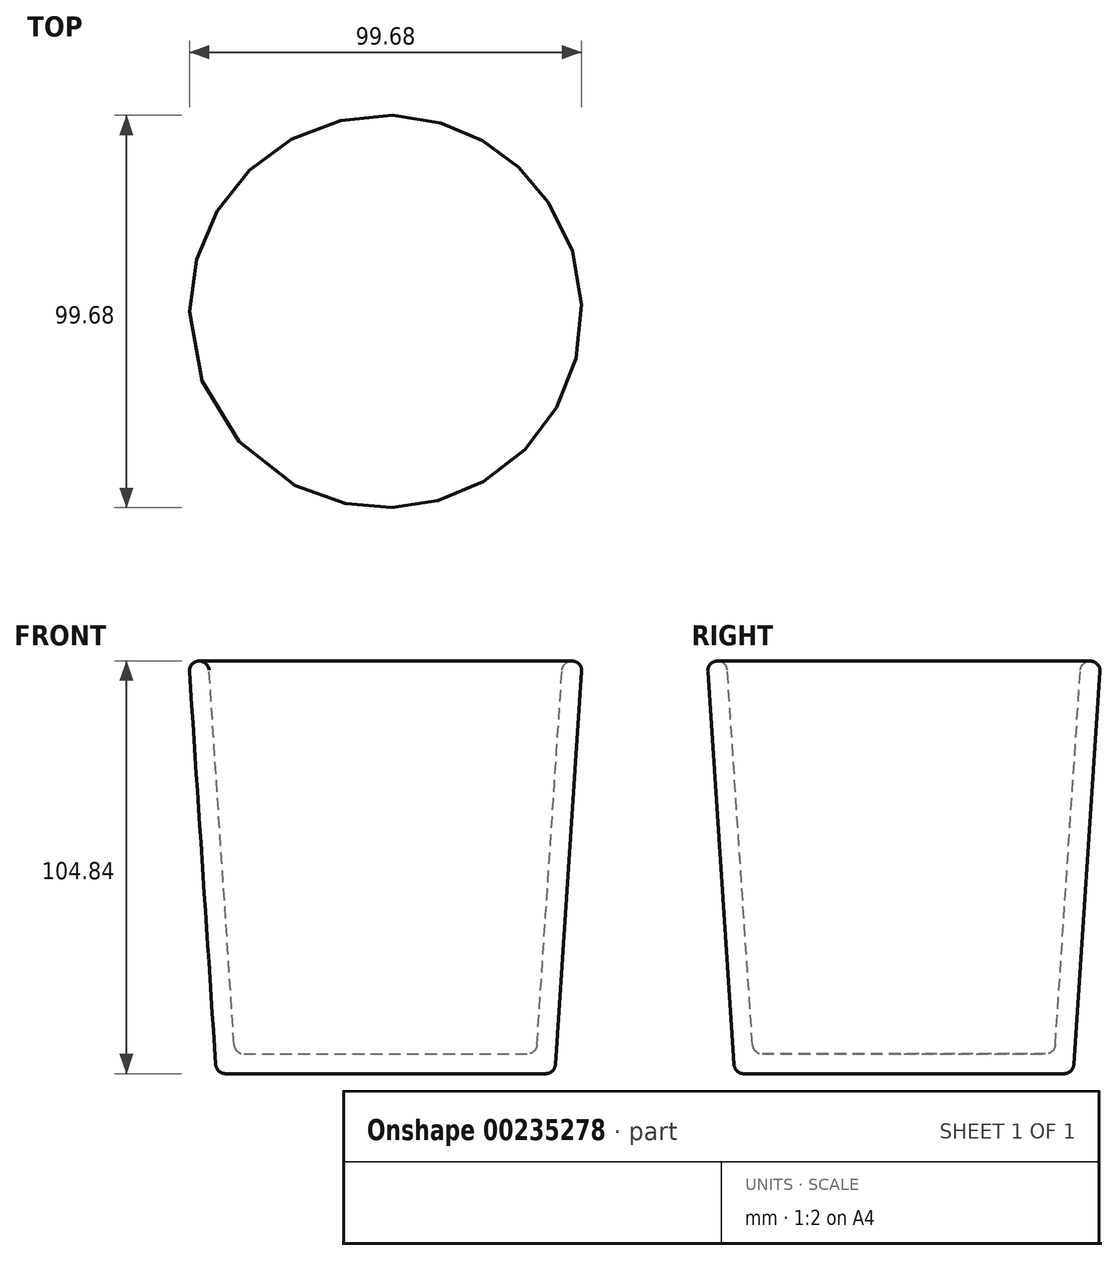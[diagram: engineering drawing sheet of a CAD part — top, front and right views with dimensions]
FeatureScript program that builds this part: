
annotation { "Feature Type Name" : "Feature", "Feature Type Description" : "" }
export const myFeature = defineFeature(function(context is Context, id is Id, definition is map)
    precondition{}
    {
        {
            var Q0;
            Q0=qCreatedBy(makeId("Front.planeOp"),FACE);
            var sketch = newSketch(context, id + "F0", { "sketchPlane" : qUnion([Q0])});
            skLineSegment(sketch, "E0", {"start": v(0, 0) * mm, "end": v(43, 0) * mm});
            skLineSegment(sketch, "E1", {"start": v(43, 0) * mm, "end": v(50, 104.67) * mm});
            skLineSegment(sketch, "E2", {"start": v(50, 104.67) * mm, "end": v(45.01, 105) * mm});
            skLineSegment(sketch, "E3", {"start": v(45.01, 105) * mm, "end": v(38.32, 5) * mm});
            skLineSegment(sketch, "E4", {"start": v(38.32, 5) * mm, "end": v(0, 5) * mm});
            skLineSegment(sketch, "E5", {"start": v(0, 5) * mm, "end": v(0, 0) * mm});
            skSolve(sketch);
        }
        {
            var Q0;
            Q0 = qSketchRegion(id + "F0", true);
            var Q1;
            Q1=sQuery(id+"F0.wireOp",EDGE,"E5");
            revolve(context, id + "F1", {"entities" : qUnion([Q0]), "axis" : qUnion([Q1]), "revolveType" : RevolveType.FULL});
        }
        {
            var Q0;
            Q0=makeQuery(id+"F1.opRevolve","SWEPT_EDGE",EDGE,{"disambiguationData":[OSD([sQuery(id+"F0.wireOp",EDGE,"E1"),sQuery(id+"F0.wireOp",EDGE,"E2")])]});
            var Q1;
            Q1=makeQuery(id+"F1.opRevolve","SWEPT_EDGE",EDGE,{"disambiguationData":[OSD([sQuery(id+"F0.wireOp",EDGE,"E2"),sQuery(id+"F0.wireOp",EDGE,"E3")])]});
            var Q2;
            Q2=makeQuery(id+"F1.opRevolve","SWEPT_EDGE",EDGE,{"disambiguationData":[OSD([sQuery(id+"F0.wireOp",EDGE,"E0"),sQuery(id+"F0.wireOp",EDGE,"E1")])]});
            var Q3;
            Q3=makeQuery(id+"F1.opRevolve","SWEPT_EDGE",EDGE,{"disambiguationData":[OSD([sQuery(id+"F0.wireOp",EDGE,"E3"),sQuery(id+"F0.wireOp",EDGE,"E4")])]});
            fillet(context, id + "F2", {"entities" : qUnion([Q0, Q1, Q2, Q3]), "radius" : 2.5 * mm, "tangentPropagation" : true, "allowEdgeOverflow" : false});
        }
    });
